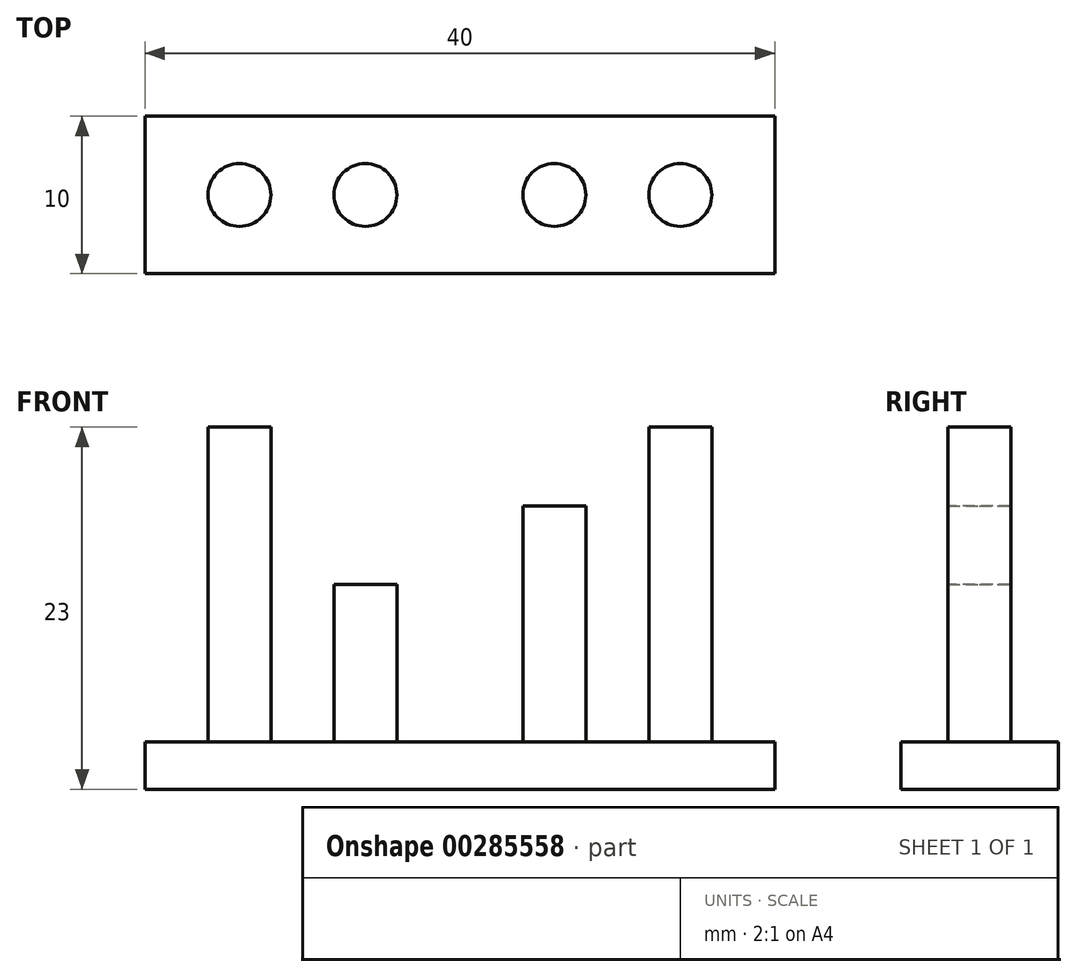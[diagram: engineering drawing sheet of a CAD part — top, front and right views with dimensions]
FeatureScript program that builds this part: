
annotation { "Feature Type Name" : "Feature", "Feature Type Description" : "" }
export const myFeature = defineFeature(function(context is Context, id is Id, definition is map)
    precondition{}
    {
        {
            var Q0;
            Q0=qCreatedBy(makeId("Top.planeOp"),FACE);
            var sketch = newSketch(context, id + "F0", { "sketchPlane" : qUnion([Q0])});
            skLineSegment(sketch, "E0.bottom", {"start": v(20, -5) * mm, "end": v(-20, -5) * mm});
            skLineSegment(sketch, "E0.top", {"start": v(20, 5) * mm, "end": v(-20, 5) * mm});
            skLineSegment(sketch, "E0.left", {"start": v(20, -5) * mm, "end": v(20, 5) * mm});
            skLineSegment(sketch, "E0.right", {"start": v(-20, -5) * mm, "end": v(-20, 5) * mm});
            skPoint(sketch, "E0.middle", {"position": v(0, 0) * mm});
            skSolve(sketch);
        }
        {
            var Q0;
            Q0 = qSketchRegion(id + "F0", true);
            extrude(context, id + "F1", {"entities" : qUnion([Q0]), "depth" : 3 * mm});
        }
        {
            var Q0;
            Q0=makeQuery(id+"F1.opExtrude","CAP_FACE",FACE,{"disambiguationData":[OSD([sQuery(id+"F0.wireOp",EDGE,"E0.bottom"),sQuery(id+"F0.wireOp",EDGE,"E0.top"),sQuery(id+"F0.wireOp",EDGE,"E0.left"),sQuery(id+"F0.wireOp",EDGE,"E0.right")])],"isStart":false});
            var sketch = newSketch(context, id + "F2", { "sketchPlane" : qUnion([Q0])});
            skCircle(sketch, "E1", {"center": v(-14, 0) * mm, "radius": 2 * mm});
            skPoint(sketch, "E1.centerSnap0", {"position": v(-20, 0) * mm});
            skCircle(sketch, "E2", {"center": v(14, 0) * mm, "radius": 2 * mm});
            skPoint(sketch, "E2.centerSnap0", {"position": v(20, 0) * mm});
            skCircle(sketch, "E3", {"center": v(-6, 0) * mm, "radius": 2 * mm});
            skCircle(sketch, "E4", {"center": v(6, 0) * mm, "radius": 2 * mm});
            skSolve(sketch);
        }
        {
            var Q0;
            Q0=makeQuery(id+"F2.imprint","IMPRINT",FACE,{"disambiguationData":[TD([[makeQuery(id+"F2.imprint","IMPRINT",EDGE,{"derivedFrom":sQuery(id+"F2.wireOp",EDGE,"E1")}),1.0]])]});
            var Q1;
            Q1=makeQuery(id+"F2.imprint","IMPRINT",FACE,{"disambiguationData":[TD([[makeQuery(id+"F2.imprint","IMPRINT",EDGE,{"derivedFrom":sQuery(id+"F2.wireOp",EDGE,"E2")}),1.0]])]});
            extrude(context, id + "F3", {"entities" : qUnion([Q0, Q1]), "operationType" : NewBodyOperationType.ADD, "depth" : 20 * mm});
        }
        {
            var Q0;
            Q0=makeQuery(id+"F2.imprint","IMPRINT",FACE,{"disambiguationData":[TD([[makeQuery(id+"F2.imprint","IMPRINT",EDGE,{"derivedFrom":sQuery(id+"F2.wireOp",EDGE,"E3")}),1.0]])]});
            extrude(context, id + "F4", {"entities" : qUnion([Q0]), "operationType" : NewBodyOperationType.ADD, "depth" : 10 * mm});
        }
        {
            var Q0;
            Q0=makeQuery(id+"F2.imprint","IMPRINT",FACE,{"disambiguationData":[TD([[makeQuery(id+"F2.imprint","IMPRINT",EDGE,{"derivedFrom":sQuery(id+"F2.wireOp",EDGE,"E4")}),1.0]])]});
            var Q1;
            Q1=sQuery(id+"F2.wireOp",EDGE,"E4");
            extrude(context, id + "F5", {"entities" : qUnion([Q0]), "operationType" : NewBodyOperationType.ADD, "surfaceEntities" : qUnion([Q1]), "depth" : 15 * mm});
        }
    });
